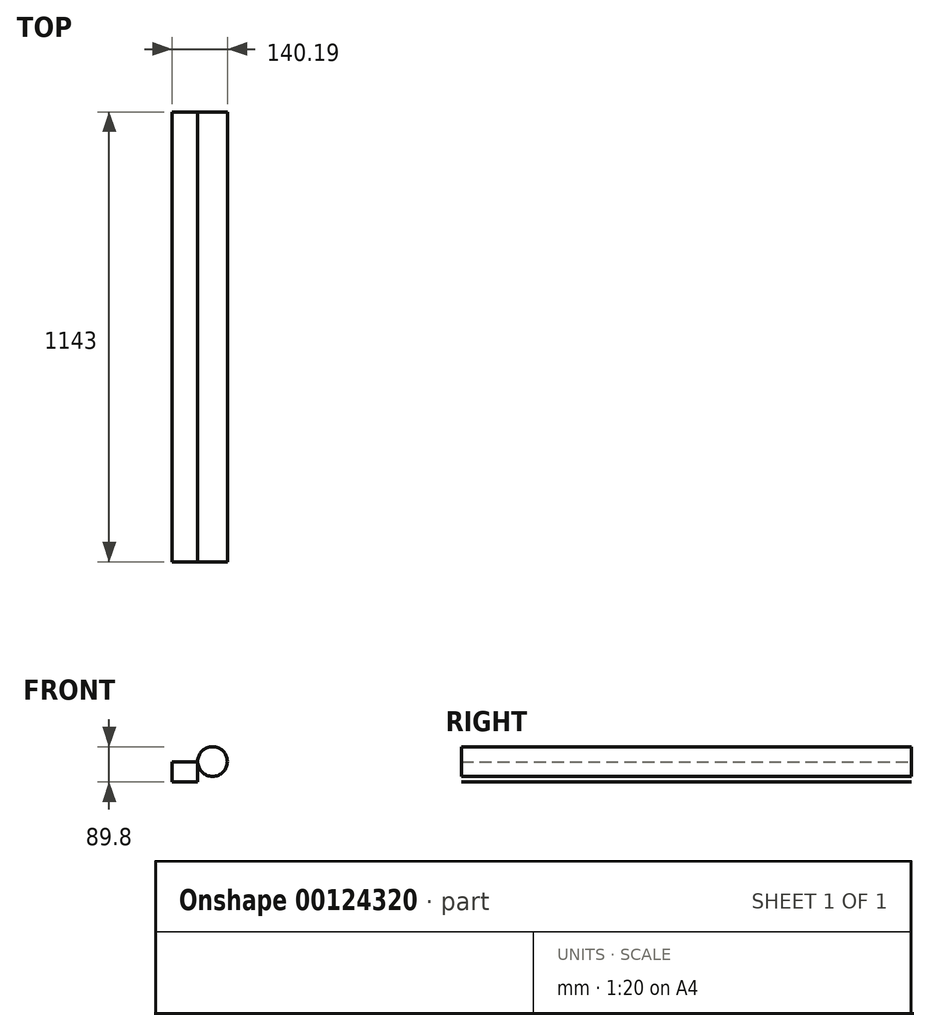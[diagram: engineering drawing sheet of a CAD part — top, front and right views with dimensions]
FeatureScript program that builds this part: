
annotation { "Feature Type Name" : "Feature", "Feature Type Description" : "" }
export const myFeature = defineFeature(function(context is Context, id is Id, definition is map)
    precondition{}
    {
        {
            var Q0;
            Q0=qCreatedBy(makeId("Front.planeOp"),FACE);
            var sketch = newSketch(context, id + "F0", { "sketchPlane" : qUnion([Q0])});
            skCircle(sketch, "E0", {"center": v(31.23, 8.1) * mm, "radius": 37.65 * mm});
            skLineSegment(sketch, "E1.bottom", {"start": v(-6.41, 7.56) * mm, "end": v(-71.3, 7.56) * mm});
            skLineSegment(sketch, "E1.top", {"start": v(-6.41, -44.05) * mm, "end": v(-71.3, -44.05) * mm});
            skLineSegment(sketch, "E1.left", {"start": v(-6.41, 7.56) * mm, "end": v(-6.41, -44.05) * mm});
            skLineSegment(sketch, "E1.right", {"start": v(-71.3, 7.56) * mm, "end": v(-71.3, -44.05) * mm});
            skSolve(sketch);
        }
        {
            var Q0;
            Q0 = qSketchRegion(id + "F0", true);
            var Q1;
            Q1=makeQuery(id+"F0.imprint","IMPRINT",FACE,{"disambiguationData":[TD([[makeQuery(id+"F0.imprint","IMPRINT",EDGE,{"derivedFrom":sQuery(id+"F0.wireOp",EDGE,"E0")}),1.0]])]});
            var Q2;
            Q2=makeQuery(id+"F0.imprint","IMPRINT",FACE,{"disambiguationData":[TD([[makeQuery(id+"F0.imprint","IMPRINT",EDGE,{"derivedFrom":sQuery(id+"F0.wireOp",EDGE,"E1.bottom")}),1.0]])]});
            extrude(context, id + "F1", {"entities" : qUnion([Q0, Q1, Q2]), "depth" : 1143 * mm});
        }
    });
